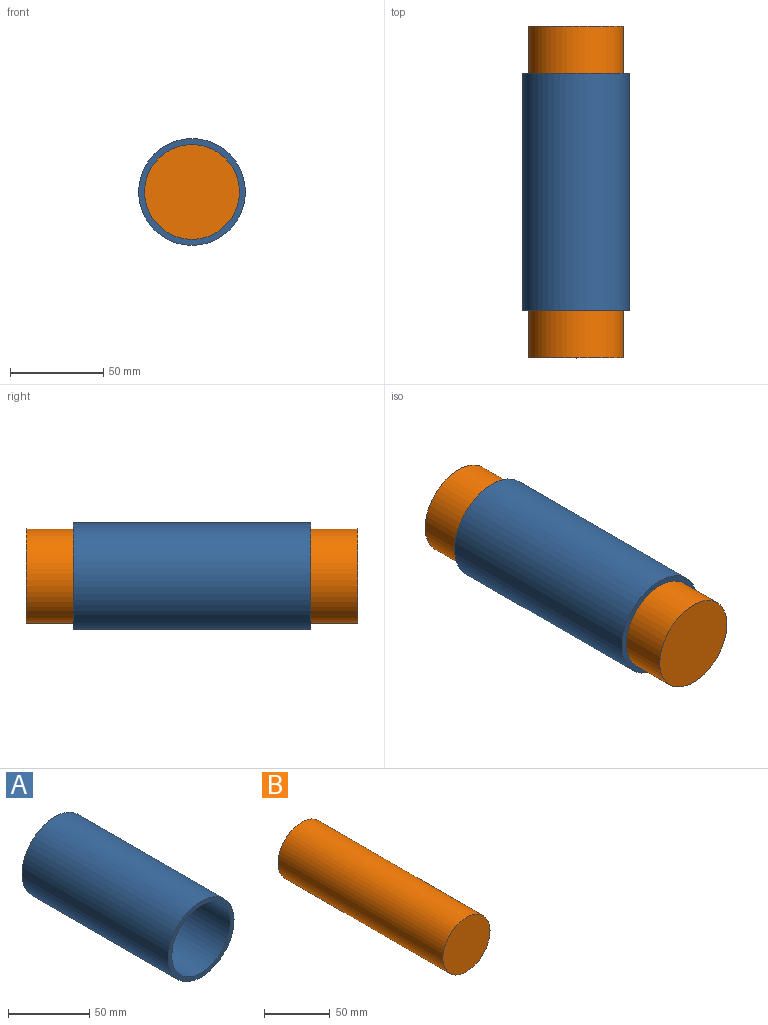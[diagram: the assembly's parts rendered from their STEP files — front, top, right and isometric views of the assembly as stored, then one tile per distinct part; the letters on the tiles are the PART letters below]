
ASSEMBLY  parts=2 mates=1
PART A: 4 faces, bbox 57.2x127x57.2 mm
  f0: cylinder r=25.4mm len=127mm, axis (0,-1,0), area 20268.3mm2, adj f2,f3
  f1: cylinder r=28.57mm len=127mm, axis (0,-1,0), area 22801.8mm2, adj f2,f3
  f2: plane 57.15x57.15mm, normal (0,1,0), area 538.4mm2, adj f0,f1
  f3: plane 57.15x57.15mm, normal (0,-1,0), area 538.4mm2, adj f0,f1
PART B: 3 faces, bbox 50.8x177.8x50.8 mm
  f0: cylinder r=25.4mm len=177.8mm, axis (0,1,0), area 28375.6mm2, adj f1,f2
  f1: plane 50.8x50.8mm, normal (0,-1,0), area 2026.8mm2, adj f0
  f2: plane 50.8x50.8mm, normal (0,1,0), area 2026.8mm2, adj f0
PLACE A t=(-8.71,-127.1,55.52)mm
PLACE B t=(-99.61,25.3,43.92)mm
MATE revolute A.f1 <-> B.f0  axis (0,-1,0) through (-8.71,-63.6,55.52)mm
